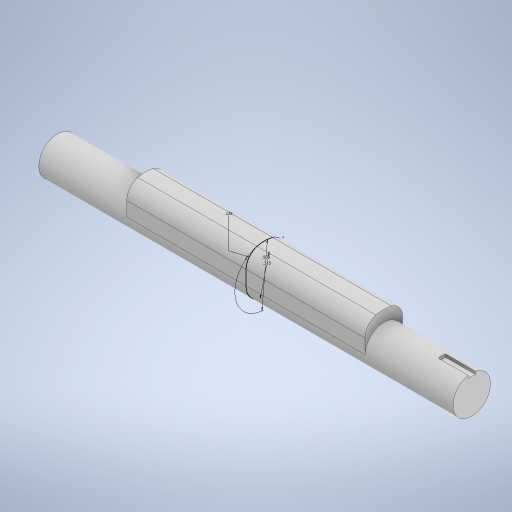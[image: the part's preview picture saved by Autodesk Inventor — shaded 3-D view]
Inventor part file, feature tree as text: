
AUTODESK INVENTOR PART (.ipt)
format: ipt  version: 2023 (Build 270158000, 158)  size: 258,560 bytes
history: native  units: in
note: dims shown in document units (in); Inventor stores cm internally (conversion verified against a paired STEP export)
features: extrude x3, sketch x2
ambient origin geometry x8: Origin, YZ Plane, XZ Plane, XY Plane, X Axis, Y Axis, Z Axis, Center Point
bodies: Solid1 (feature_tree)
feature tree (5):
  sketch  "Sketch1"  dims[d0=0.315in d1=0.5in]
  extrude  "Extrusion1"  Depth=0.315in
  extrude  "Extrusion2"  Depth=3.476in TaperAngle=0.0deg
  extrude  "Extrusion3"  Depth=2.0in TaperAngle=0.0deg
  sketch  "Sketch2"  dims[d2=0.125in d3=3.476in d4=0.0in d5=2.0in d6=0.0in d7=0.25in d8=0.0in]
